# Revit family: Deca_Válvula de descarga Hydra Duo_2545
name_source: partatom
category: Plumbing Fixtures
units: mm (PartAtom-declared; Revit-internal decimal feet)

## family parameters
Cut with Voids When Loaded = No
Host = Face
Part Type = Normal
Room Calculation Point = No
Round Connector Dimension = Use Diameter
Shared = No

## types (2) — shared parameters
Acompanha o Produto = -
Aprovado por = quattroD
Atendimento ao Cliente = 0800-0117073
Categoria = SISTEMAS DE DESCARGA
Composição Anel Vedação = -
Composição Assento = -
Composição Básica = Liga de Cobre (bronze e latão),Plásticos de Engenharia,Elastômeros
Composição Componente = -
Consumo = 6 / 3 (lpf) - 1,6 / 0,8 (gpf)
Cor Interna = -
Cor Principal = Cromado
Cor Secundária = -
Cores Componente = -
Criado por = quattroD
Código Pai = 2545
Default Elevation = 1100 mm
Diâmetro Água Fria Saída = 40 mm  [stored 0.131234 ft]
Informações Complementares = -
Itens de Instalação = -
Linha = Hydra Duo
Manufacturer = Deca
Material = Deca_Cromado
Norma = NBR15857
Pressão máx. funcionamento = 40 MCA
Pressão mín. Aquec. Acúmulo = -
Pressão mín. Aquec. Passagem = -
Raio Água Fria Saída = 20 mm  [stored 0.0656168 ft]
Saída de Esgoto = -
Segmento = Válvula Hydra
Tipo de dispositivo economizador = -
Tipo de mecanismo utilizado = -
Tipo de rosca de entrada = BSP NBR 8133
Tipo de rosca de saída = BSP NBR 8133
URL = www.deca.com.br
Vazão na Pressão máx. (L/min) = -
Vazão na Pressão mín. (L/min) = -

## per-type parameters (varying)
| type | Description | Diâmetro Água Fria | Model | Peso Líquido (Kg) | Pressão mín. funcionamento | Raio Água Fria |
| 2545.C.112_Cromado_DN15 | Válvula de descarga 1 1/2" | 15 mm  [stored 0.0492126 ft] | 2545.C.112 | 1.15 | 2 MCA | 8 mm  [stored 0.0262467 ft] |
| 2545.C.114_Cromado_DN32 | Válvula de descarga 1 1/4" | 32 mm  [stored 0.104987 ft] | 2545.C.114 | 1.101 | 10 MCA | 16 mm  [stored 0.0524934 ft] |

note: [stored X ft] marks values corroborated as IEEE doubles in the binary element streams (Revit-internal decimal feet)

## geometry (parser evidence)
native form markers: Sweep x1
no freeform markers — native parametric forms only
